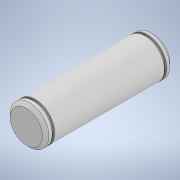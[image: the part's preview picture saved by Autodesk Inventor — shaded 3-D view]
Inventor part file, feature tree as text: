
AUTODESK INVENTOR PART (.ipt)
format: ipt  version: 2022 (Build 260153000, 153)  size: 128,000 bytes
history: native  units: mm
features: revolve x1, sketch x1
ambient origin geometry x8: Origin, YZ Plane, XZ Plane, XY Plane, X Axis, Y Axis, Z Axis, Center Point
bodies: Solid1 (feature_tree)
feature tree (2):
  revolve  "Revolution1"  [1 undecoded]
  sketch  "Sketch1"  dims[d0=6.0mm d1=17.0mm d2=0.7mm d3=0.5mm d7=2.0mm d8=1.0mm d9=1.0mm d10=90.0deg]
note: 1 required parameter value undecoded (feature->parameter linkage not recoverable at this tier; creation-order binding heuristic only, values carry confidence <= 0.55)
